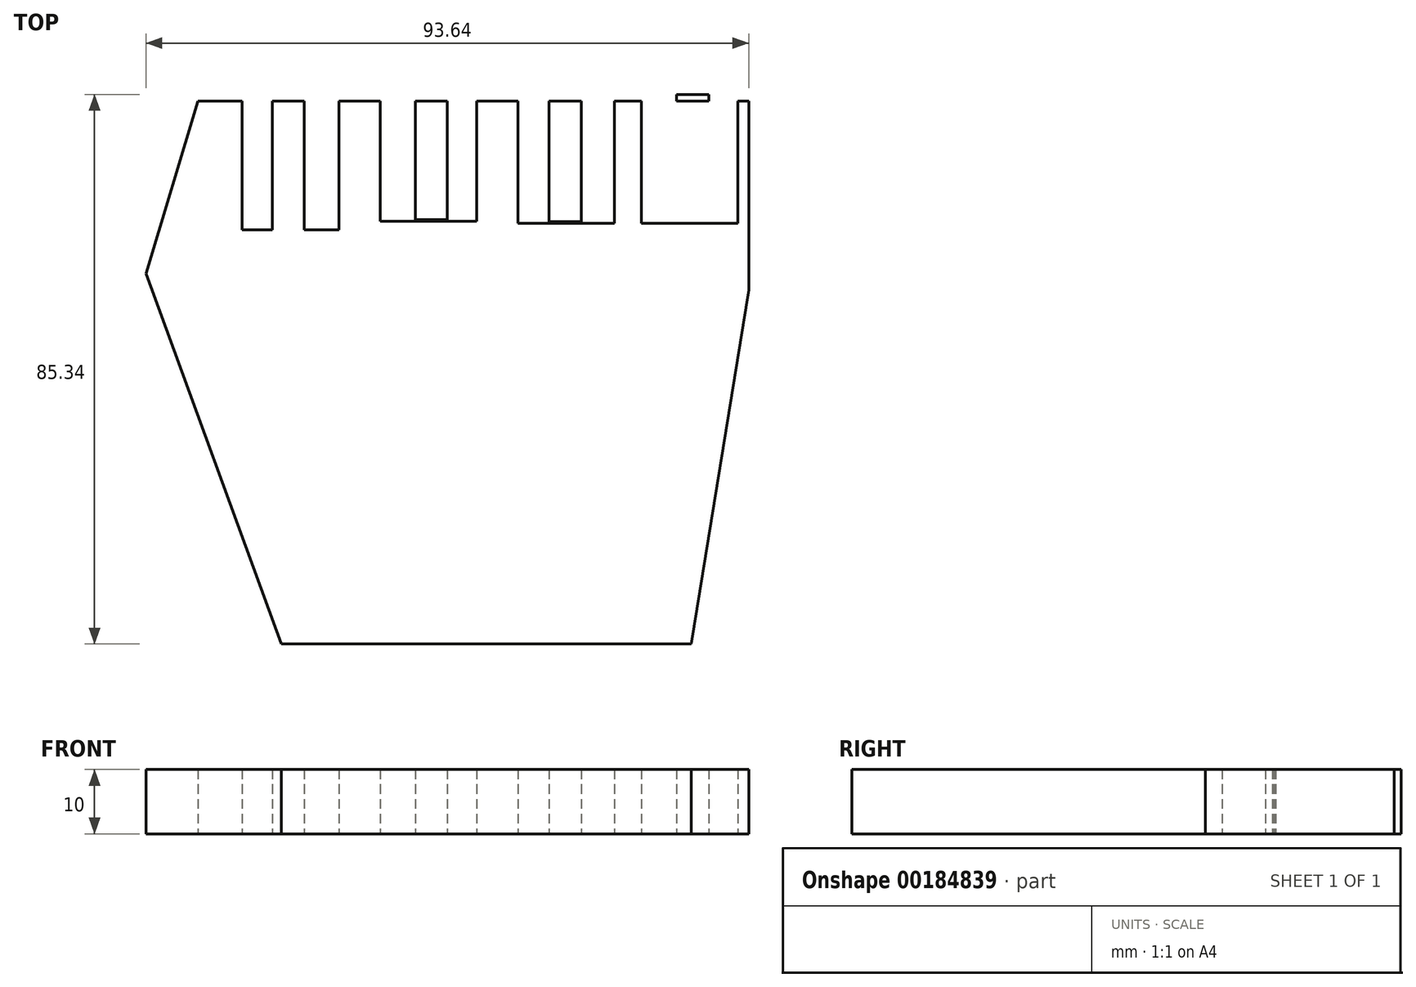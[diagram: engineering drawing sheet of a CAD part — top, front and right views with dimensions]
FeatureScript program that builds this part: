
annotation { "Feature Type Name" : "Feature", "Feature Type Description" : "" }
export const myFeature = defineFeature(function(context is Context, id is Id, definition is map)
    precondition{}
    {
        {
            var Q0;
            Q0=qCreatedBy(makeId("Top.planeOp"),FACE);
            var sketch = newSketch(context, id + "F0", { "sketchPlane" : qUnion([Q0])});
            skLineSegment(sketch, "E0.bottom", {"start": v(11.33, -0.6) * mm, "end": v(18.2, -0.6) * mm});
            skLineSegment(sketch, "E0.top", {"start": v(24.27, -84.92) * mm, "end": v(87.98, -84.92) * mm});
            skLineSegment(sketch, "E0.right", {"start": v(96.9, -0.6) * mm, "end": v(96.9, -29.94) * mm});
            skLineSegment(sketch, "E1", {"start": v(11.33, -0.6) * mm, "end": v(3.26, -27.37) * mm});
            skLineSegment(sketch, "E2", {"start": v(3.26, -27.37) * mm, "end": v(24.27, -84.92) * mm});
            skLineSegment(sketch, "E3", {"start": v(96.9, -29.94) * mm, "end": v(87.98, -84.92) * mm});
            skLineSegment(sketch, "E4.bottom", {"start": v(22.85, -0.6) * mm, "end": v(27.85, -0.6) * mm});
            skLineSegment(sketch, "E4.top", {"start": v(18.2, -20.6) * mm, "end": v(33.2, -20.6) * mm});
            skLineSegment(sketch, "E4.left", {"start": v(18.2, -0.6) * mm, "end": v(18.2, -20.6) * mm});
            skLineSegment(sketch, "E4.right", {"start": v(33.2, -0.6) * mm, "end": v(33.2, -20.6) * mm});
            skLineSegment(sketch, "E5.bottom", {"start": v(45.08, 0.73) * mm, "end": v(50.08, 0.73) * mm});
            skLineSegment(sketch, "E5.top", {"start": v(39.64, -19.27) * mm, "end": v(54.64, -19.27) * mm});
            skLineSegment(sketch, "E5.left", {"start": v(39.64, 0.73) * mm, "end": v(39.64, -19.27) * mm});
            skLineSegment(sketch, "E5.right", {"start": v(54.64, 0.73) * mm, "end": v(54.64, -19.27) * mm});
            skLineSegment(sketch, "E6.bottom", {"start": v(65.89, 0.42) * mm, "end": v(70.89, 0.42) * mm});
            skLineSegment(sketch, "E6.top", {"start": v(61.03, -19.58) * mm, "end": v(76.03, -19.58) * mm});
            skLineSegment(sketch, "E6.left", {"start": v(61.03, 0.42) * mm, "end": v(61.03, -19.58) * mm});
            skLineSegment(sketch, "E6.right", {"start": v(76.03, 0.42) * mm, "end": v(76.03, -19.58) * mm});
            skLineSegment(sketch, "E7.bottom", {"start": v(85.7, 0.42) * mm, "end": v(90.7, 0.42) * mm});
            skLineSegment(sketch, "E7.top", {"start": v(80.22, -19.58) * mm, "end": v(95.22, -19.58) * mm});
            skLineSegment(sketch, "E7.left", {"start": v(80.22, 0.42) * mm, "end": v(80.22, -19.58) * mm});
            skLineSegment(sketch, "E7.right", {"start": v(95.22, 0.42) * mm, "end": v(95.22, -19.58) * mm});
            skLineSegment(sketch, "E8.top", {"start": v(85.7, -19.58) * mm, "end": v(90.7, -19.58) * mm});
            skLineSegment(sketch, "E8.left", {"start": v(85.7, 0.42) * mm, "end": v(85.7, -19.58) * mm});
            skLineSegment(sketch, "E8.right", {"start": v(90.7, 0.42) * mm, "end": v(90.7, -19.58) * mm});
            skLineSegment(sketch, "E9.top", {"start": v(22.85, -20.6) * mm, "end": v(27.85, -20.6) * mm});
            skLineSegment(sketch, "E9.left", {"start": v(22.85, -0.6) * mm, "end": v(22.85, -20.6) * mm});
            skLineSegment(sketch, "E9.right", {"start": v(27.85, -0.6) * mm, "end": v(27.85, -20.6) * mm});
            skLineSegment(sketch, "E10.bottom", {"start": v(45.08, 0.97) * mm, "end": v(50.08, 0.97) * mm});
            skLineSegment(sketch, "E10.top", {"start": v(45.08, -19.03) * mm, "end": v(50.08, -19.03) * mm});
            skLineSegment(sketch, "E10.left", {"start": v(45.08, 0.97) * mm, "end": v(45.08, -19.03) * mm});
            skLineSegment(sketch, "E10.right", {"start": v(50.08, 0.97) * mm, "end": v(50.08, -19.03) * mm});
            skLineSegment(sketch, "E11.bottom", {"start": v(65.89, 0.66) * mm, "end": v(70.89, 0.66) * mm});
            skLineSegment(sketch, "E11.top", {"start": v(65.89, -19.34) * mm, "end": v(70.89, -19.34) * mm});
            skLineSegment(sketch, "E11.left", {"start": v(65.89, 0.66) * mm, "end": v(65.89, -19.34) * mm});
            skLineSegment(sketch, "E11.right", {"start": v(70.89, 0.66) * mm, "end": v(70.89, -19.34) * mm});
            skLineSegment(sketch, "E12.trimOffspring", {"start": v(33.2, -0.6) * mm, "end": v(39.64, -0.6) * mm});
            skLineSegment(sketch, "E13.trimOffspring", {"start": v(45.08, -0.6) * mm, "end": v(50.08, -0.6) * mm});
            skLineSegment(sketch, "E14.trimOffspring", {"start": v(54.64, -0.6) * mm, "end": v(61.03, -0.6) * mm});
            skLineSegment(sketch, "E15.trimOffspring", {"start": v(65.89, -0.6) * mm, "end": v(70.89, -0.6) * mm});
            skLineSegment(sketch, "E16.trimOffspring", {"start": v(76.03, -0.6) * mm, "end": v(80.22, -0.6) * mm});
            skLineSegment(sketch, "E17.trimOffspring", {"start": v(85.7, -0.6) * mm, "end": v(90.7, -0.6) * mm});
            skLineSegment(sketch, "E18.trimOffspring", {"start": v(95.22, -0.6) * mm, "end": v(96.9, -0.6) * mm});
            skSolve(sketch);
        }
        {
            var Q0;
            {var subQ5=sQuery(id+"F0.wireOp",EDGE,"E10.top");Q0=makeQuery(id+"F0.imprint","IMPRINT",FACE,{"disambiguationData":[TD([[makeQuery(id+"F0.imprint","IMPRINT",EDGE,{"derivedFrom":subQ5}),1.0]])]});}
            var Q1;
            Q1=makeQuery(id+"F0.imprint","IMPRINT",FACE,{"disambiguationData":[TD([[makeQuery(id+"F0.imprint","IMPRINT",EDGE,{"derivedFrom":sQuery(id+"F0.wireOp",EDGE,"E4.bottom")}),-1.0]])]});
            var Q2;
            {var subQ5=sQuery(id+"F0.wireOp",EDGE,"E11.top");Q2=makeQuery(id+"F0.imprint","IMPRINT",FACE,{"disambiguationData":[TD([[makeQuery(id+"F0.imprint","IMPRINT",EDGE,{"derivedFrom":subQ5}),1.0]])]});}
            var Q3;
            Q3=makeQuery(id+"F0.imprint","IMPRINT",FACE,{"disambiguationData":[TD([[makeQuery(id+"F0.imprint","IMPRINT",EDGE,{"derivedFrom":sQuery(id+"F0.wireOp",EDGE,"E0.top")}),1.0]])]});
            var Q4;
            Q4=makeQuery(id+"F0.imprint","IMPRINT",FACE,{"disambiguationData":[TD([[makeQuery(id+"F0.imprint","IMPRINT",EDGE,{"derivedFrom":sQuery(id+"F0.wireOp",EDGE,"E7.bottom")}),-1.0]])]});
            extrude(context, id + "F1", {"entities" : qUnion([Q0, Q1, Q2, Q3, Q4]), "depth" : 10 * mm});
        }
    });
